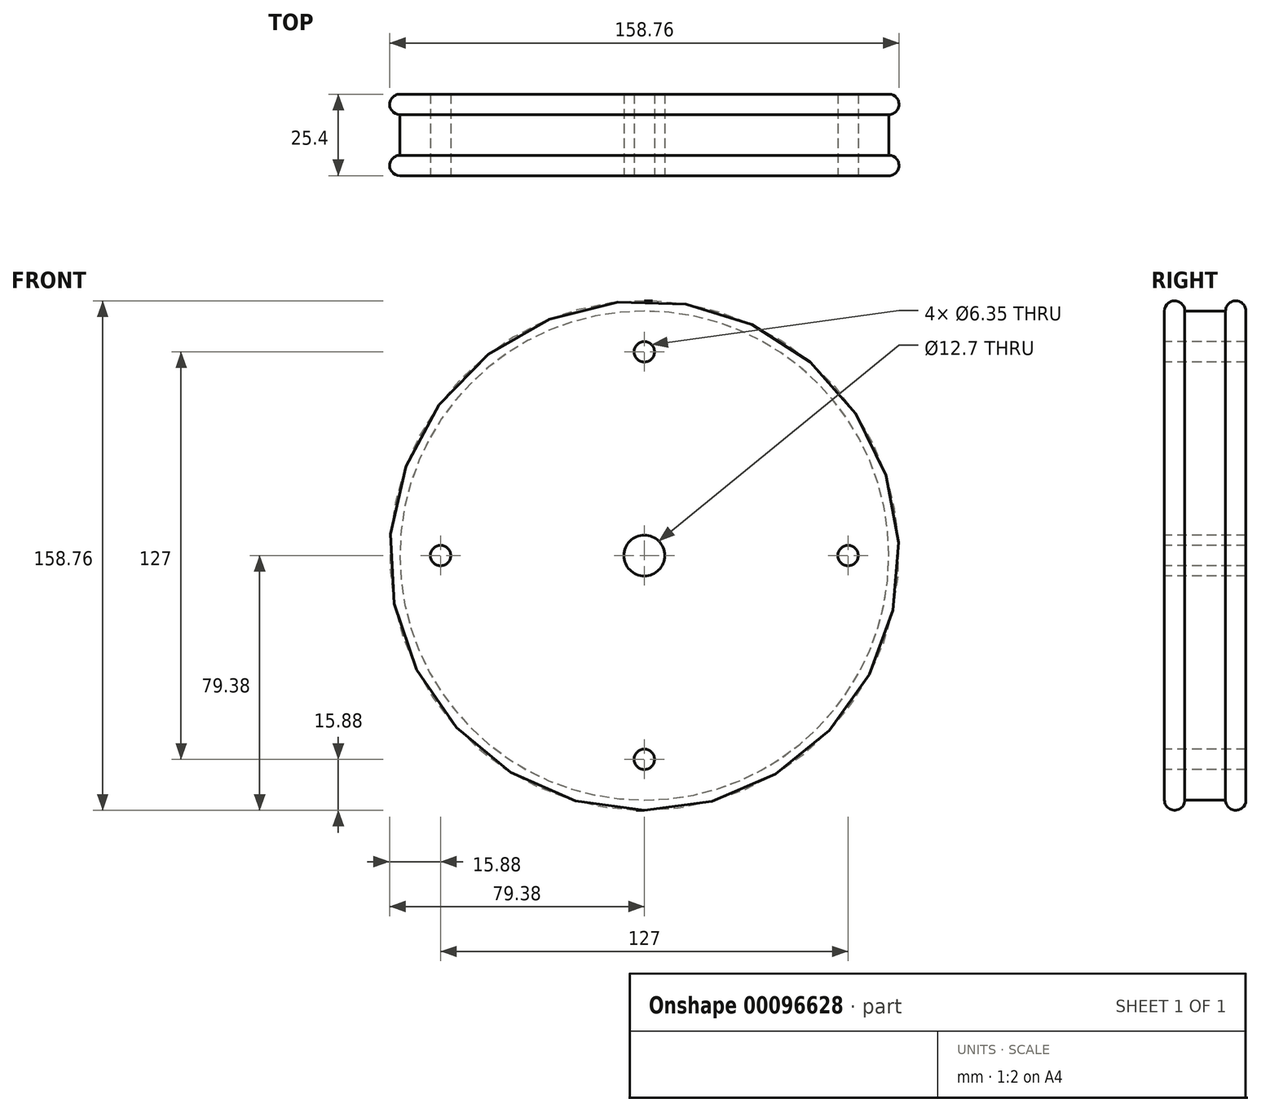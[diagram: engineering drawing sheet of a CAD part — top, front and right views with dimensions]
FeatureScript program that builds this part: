
annotation { "Feature Type Name" : "Feature", "Feature Type Description" : "" }
export const myFeature = defineFeature(function(context is Context, id is Id, definition is map)
    precondition{}
    {
        {
            var Q0;
            Q0=qCreatedBy(makeId("Front.planeOp"),FACE);
            var sketch = newSketch(context, id + "F0", { "sketchPlane" : qUnion([Q0])});
            skCircle(sketch, "E0", {"center": v(0, 0) * mm, "radius": 76.2 * mm});
            skSolve(sketch);
        }
        {
            var Q0;
            Q0 = qSketchRegion(id + "F0", true);
            extrude(context, id + "F1", {"entities" : qUnion([Q0]), "depth" : 12.7 * mm});
        }
        {
            var Q0;
            Q0=makeQuery(id+"F1.opExtrude","CAP_FACE",FACE,{"disambiguationData":[OSD([sQuery(id+"F0.wireOp",EDGE,"E0")])],"isStart":false});
            var sketch = newSketch(context, id + "F2", { "sketchPlane" : qUnion([Q0])});
            skCircle(sketch, "E1", {"center": v(0, 0) * mm, "radius": 79.38 * mm});
            skSolve(sketch);
        }
        {
            var Q0;
            Q0 = qSketchRegion(id + "F2", true);
            extrude(context, id + "F3", {"entities" : qUnion([Q0]), "operationType" : NewBodyOperationType.ADD, "depth" : 6.35 * mm});
        }
        {
            var Q0;
            Q0=makeQuery(id+"F1.opExtrude","CAP_FACE",FACE,{"disambiguationData":[OSD([sQuery(id+"F0.wireOp",EDGE,"E0")])],"isStart":true});
            var sketch = newSketch(context, id + "F4", { "sketchPlane" : qUnion([Q0])});
            skCircle(sketch, "E2.0", {"center": v(0, 0) * mm, "radius": 79.38 * mm});
            skSolve(sketch);
        }
        {
            var Q0;
            Q0 = qSketchRegion(id + "F4", true);
            extrude(context, id + "F5", {"entities" : qUnion([Q0]), "operationType" : NewBodyOperationType.ADD, "depth" : 6.35 * mm});
        }
        {
            var Q0;
            Q0=makeQuery(id+"F3.opExtrude","CAP_FACE",FACE,{"disambiguationData":[OSD([sQuery(id+"F2.wireOp",EDGE,"E1")])],"isStart":false});
            var sketch = newSketch(context, id + "F6", { "sketchPlane" : qUnion([Q0])});
            skPoint(sketch, "E3", {"position": v(0, 0) * mm});
            skSolve(sketch);
        }
        {
            var Q0;
            Q0=sQuery(id+"F6.wireOp",VERTEX,"E3");
            var Q1;
            Q1=makeQuery(id+"F1.opExtrude","SWEPT_BODY",BODY,{"disambiguationData":[OSD([sQuery(id+"F0.wireOp",EDGE,"E0")])]});
            hole(context, id + "F7", {"style" : HoleStyle.SIMPLE, "endStyle" : HoleEndStyle.THROUGH, "holeDiameter" : 12.7 * mm, "locations" : qUnion([Q0]), "scope" : qUnion([Q1]), "isTappedThrough" : true});
        }
        {
            var Q0;
            Q0=makeQuery(id+"F3.opExtrude","CAP_FACE",FACE,{"disambiguationData":[OSD([sQuery(id+"F2.wireOp",EDGE,"E1")])],"isStart":false});
            var sketch = newSketch(context, id + "F8", { "sketchPlane" : qUnion([Q0])});
            skCircle(sketch, "E4", {"center": v(0, 63.5) * mm, "radius": 3.18 * mm});
            skCircle(sketch, "E5.1.0", {"center": v(-63.5, 0) * mm, "radius": 3.18 * mm});
            skCircle(sketch, "E5.2.0", {"center": v(0, -63.5) * mm, "radius": 3.18 * mm});
            skCircle(sketch, "E5.3.0", {"center": v(63.5, 0) * mm, "radius": 3.18 * mm});
            skPoint(sketch, "E5.center", {"position": v(0, 0) * mm});
            skSolve(sketch);
        }
        {
            var Q0;
            Q0 = qSketchRegion(id + "F8", true);
            extrude(context, id + "F9", {"entities" : qUnion([Q0]), "operationType" : NewBodyOperationType.REMOVE, "endBound" : BoundingType.THROUGH_ALL, "oppositeDirection" : true, "depth" : 25.4 * mm});
        }
        {
            var Q0;
            Q0=makeQuery(id+"F3.opExtrude","CAP_EDGE",EDGE,{"disambiguationData":[OSD([sQuery(id+"F2.wireOp",EDGE,"E1")])],"isStart":false});
            var Q1;
            Q1=makeQuery(id+"F3.opExtrude","CAP_EDGE",EDGE,{"disambiguationData":[OSD([sQuery(id+"F2.wireOp",EDGE,"E1")])],"isStart":true});
            var Q2;
            Q2=makeQuery(id+"F5.opExtrude","CAP_EDGE",EDGE,{"disambiguationData":[OSD([sQuery(id+"F4.wireOp",EDGE,"E2.0")])],"isStart":true});
            var Q3;
            Q3=makeQuery(id+"F5.opExtrude","CAP_EDGE",EDGE,{"disambiguationData":[OSD([sQuery(id+"F4.wireOp",EDGE,"E2.0")])],"isStart":false});
            fillet(context, id + "F10", {"entities" : qUnion([Q0, Q1, Q2, Q3]), "radius" : 3.17 * mm, "tangentPropagation" : true, "allowEdgeOverflow" : false});
        }
    });
